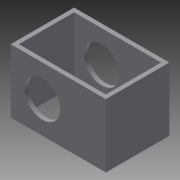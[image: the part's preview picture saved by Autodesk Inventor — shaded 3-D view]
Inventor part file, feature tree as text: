
AUTODESK INVENTOR PART (.ipt)
format: ipt  version: 2015 (Build 190159000, 159)  size: 94,720 bytes
history: native  units: in
note: dims shown in document units (in); Inventor stores cm internally (conversion verified against a paired STEP export)
features: sketch x3, extrude x2
ambient origin geometry x8: Origin, YZ Plane, XZ Plane, XY Plane, X Axis, Y Axis, Z Axis, Center Point
bodies: Solid1 (feature_tree)
feature tree (5):
  sketch  "Sketch1"  dims[d0=0.13in d1=3.0in]
  extrude  "Extrusion1"  Depth=3.0in
  extrude  "Extrusion2"  Depth=2.0in TaperAngle=0.0deg
  sketch  "Sketch2"  dims[d2=2.0in d3=2.0in d4=0.0in]
  sketch  "Sketch3"  dims[d5=1.125in d6=1.0in d7=1.0in d8=0.0in]
